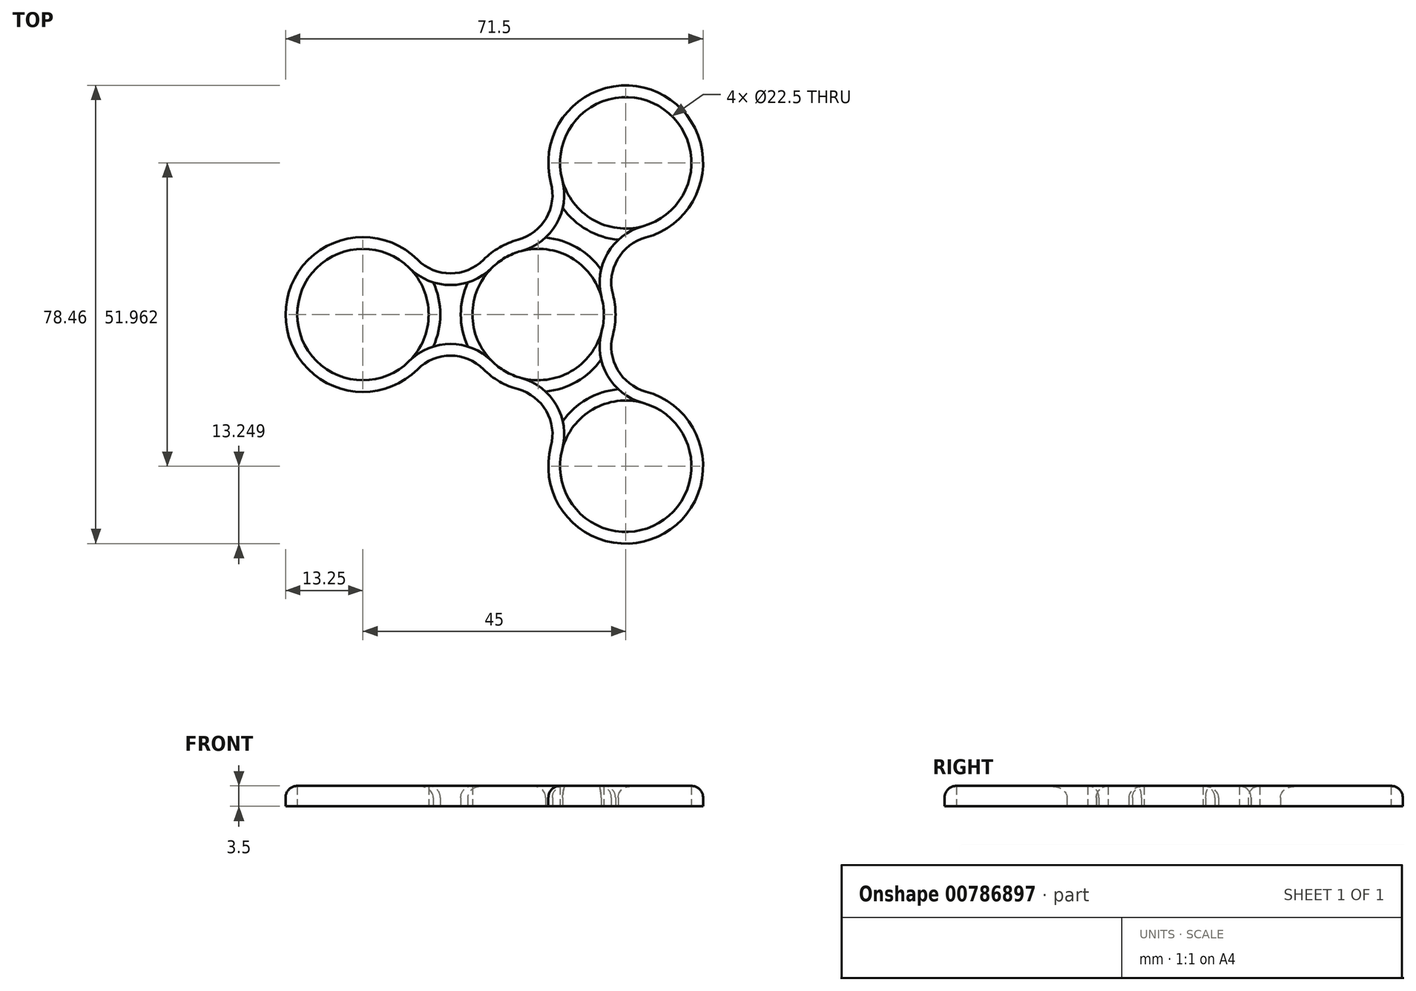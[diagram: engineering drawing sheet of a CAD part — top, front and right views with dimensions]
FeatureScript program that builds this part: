
annotation { "Feature Type Name" : "Feature", "Feature Type Description" : "" }
export const myFeature = defineFeature(function(context is Context, id is Id, definition is map)
    precondition{}
    {
        {
            assignVariable(context, id + "F0", {"name" : "B608_T", "anyValue" : 7});
        }
        {
            var Q0;
            Q0=qCreatedBy(makeId("Top.planeOp"),FACE);
            var sketch = newSketch(context, id + "F1", { "sketchPlane" : qUnion([Q0])});
            skCircle(sketch, "E0", {"center": v(0, 0) * mm, "radius": 11.25 * mm});
            skCircle(sketch, "E1.cCircle", {"center": v(0, 0) * mm, "radius": 15 * mm, "construction": true});
            skLineSegment(sketch, "E1.0", {"start": v(15, 25.98) * mm, "end": v(15, -25.98) * mm, "construction": true});
            skLineSegment(sketch, "E1.1", {"start": v(15, -25.98) * mm, "end": v(-30, 0) * mm, "construction": true});
            skLineSegment(sketch, "E1.2", {"start": v(-30, 0) * mm, "end": v(15, 25.98) * mm, "construction": true});
            skPoint(sketch, "E1.0.midPoint", {"position": v(15, 0) * mm});
            skCircle(sketch, "E2", {"center": v(-30, 0) * mm, "radius": 11.25 * mm});
            skCircle(sketch, "E3", {"center": v(15, -25.98) * mm, "radius": 11.25 * mm});
            skCircle(sketch, "E4", {"center": v(15, 25.98) * mm, "radius": 11.25 * mm});
            skPoint(sketch, "E5.orphan", {"position": v(0, -11.15) * mm});
            skPoint(sketch, "E6.orphan", {"position": v(0, 11.15) * mm});
            skArc(sketch, "E7.0", {"start": v(-17.94, -5.5) * mm, "mid": v(-16.75, 0) * mm, "end": v(-17.94, 5.5) * mm});
            skArc(sketch, "E8.0", {"start": v(2.2, -22.57) * mm, "mid": v(21.62, -37.46) * mm, "end": v(18.45, -13.19) * mm});
            skArc(sketch, "E9.0", {"start": v(18.45, 13.19) * mm, "mid": v(13.9, 39.18) * mm, "end": v(13.73, 12.8) * mm});
            skArc(sketch, "E10.0", {"start": v(-9.35, -9.39) * mm, "mid": v(-6.62, -11.47) * mm, "end": v(-3.45, -12.8) * mm});
            skLineSegment(sketch, "E11", {"start": v(-7.65, -13.25) * mm, "end": v(-7.03, -13.25) * mm});
            skLineSegment(sketch, "E12", {"start": v(-7.65, 13.25) * mm, "end": v(-7.03, 13.25) * mm});
            skLineSegment(sketch, "E13", {"start": v(-7.65, -13.25) * mm, "end": v(-7.96, -12.71) * mm});
            skLineSegment(sketch, "E14", {"start": v(15.3, 0) * mm, "end": v(15, 0.54) * mm});
            skLineSegment(sketch, "E15", {"start": v(-7.96, 12.71) * mm, "end": v(-7.65, 13.25) * mm});
            skLineSegment(sketch, "E16", {"start": v(15, -0.54) * mm, "end": v(15.3, 0) * mm});
            skPoint(sketch, "E17.orphan", {"position": v(0, -13.25) * mm});
            skPoint(sketch, "E18.orphan", {"position": v(0, 13.25) * mm});
            skCircle(sketch, "E19", {"center": v(0, 0) * mm, "radius": 8.5 * mm});
            skCircle(sketch, "E20", {"center": v(-30, 0) * mm, "radius": 8.5 * mm});
            skCircle(sketch, "E21", {"center": v(15, -25.98) * mm, "radius": 8.5 * mm});
            skCircle(sketch, "E22", {"center": v(15, 25.98) * mm, "radius": 8.5 * mm});
            skArc(sketch, "E23", {"start": v(-20.65, 9.39) * mm, "mid": v(-15, 7.05) * mm, "end": v(-9.35, 9.39) * mm});
            skArc(sketch, "E24", {"start": v(-9.35, -9.39) * mm, "mid": v(-15, -7.05) * mm, "end": v(-20.65, -9.39) * mm});
            skArc(sketch, "E25", {"start": v(-3.45, 12.8) * mm, "mid": v(1.4, 16.52) * mm, "end": v(2.2, 22.57) * mm});
            skArc(sketch, "E26", {"start": v(18.45, 13.19) * mm, "mid": v(13.6, 9.46) * mm, "end": v(12.8, 3.4) * mm});
            skArc(sketch, "E27", {"start": v(12.8, -3.4) * mm, "mid": v(13.6, -9.46) * mm, "end": v(18.45, -13.19) * mm});
            skArc(sketch, "E28", {"start": v(2.2, -22.57) * mm, "mid": v(1.4, -16.52) * mm, "end": v(-3.45, -12.8) * mm});
            skPoint(sketch, "E29.orphan", {"position": v(-30, 13.25) * mm});
            skPoint(sketch, "E30.orphan", {"position": v(-30, -13.25) * mm});
            skArc(sketch, "E31.0", {"start": v(-12.06, -5.5) * mm, "mid": v(-15, -5.05) * mm, "end": v(-17.94, -5.5) * mm});
            skArc(sketch, "E32.0", {"start": v(-17.94, 5.5) * mm, "mid": v(-15, 5.05) * mm, "end": v(-12.06, 5.5) * mm});
            skArc(sketch, "E33.trimOffspring", {"start": v(-12.06, 5.5) * mm, "mid": v(-13.25, 0) * mm, "end": v(-12.06, -5.5) * mm});
            skArc(sketch, "E34.trimOffspring", {"start": v(-20.65, 9.39) * mm, "mid": v(-43.25, 0) * mm, "end": v(-20.65, -9.39) * mm});
            skArc(sketch, "E35.trimOffspring", {"start": v(4.21, -18.29) * mm, "mid": v(3.12, -15.52) * mm, "end": v(1.27, -13.19) * mm});
            skArc(sketch, "E36.0", {"start": v(10.79, -7.7) * mm, "mid": v(11.88, -10.46) * mm, "end": v(13.73, -12.8) * mm});
            skArc(sketch, "E37.trimOffspring", {"start": v(1.27, -13.19) * mm, "mid": v(6.63, -11.47) * mm, "end": v(10.79, -7.7) * mm});
            skArc(sketch, "E38.trimOffspring", {"start": v(13.73, -12.8) * mm, "mid": v(8.38, -14.5) * mm, "end": v(4.21, -18.29) * mm});
            skArc(sketch, "E39.trimOffspring", {"start": v(12.8, -3.4) * mm, "mid": v(13.25, 0) * mm, "end": v(12.8, 3.4) * mm});
            skArc(sketch, "E40.0", {"start": v(1.27, 13.19) * mm, "mid": v(3.12, 15.52) * mm, "end": v(4.21, 18.29) * mm});
            skArc(sketch, "E41.trimOffspring", {"start": v(10.79, 7.7) * mm, "mid": v(6.62, 11.47) * mm, "end": v(1.27, 13.19) * mm});
            skArc(sketch, "E42.trimOffspring", {"start": v(13.73, 12.8) * mm, "mid": v(11.88, 10.46) * mm, "end": v(10.79, 7.7) * mm});
            skArc(sketch, "E43.trimOffspring", {"start": v(-3.45, 12.8) * mm, "mid": v(-6.63, 11.47) * mm, "end": v(-9.35, 9.39) * mm});
            skSolve(sketch);
        }
        {
            var Q0;
            Q0=makeQuery(id+"F1.imprint","IMPRINT",FACE,{"disambiguationData":[TD([[makeQuery(id+"F1.imprint","IMPRINT",EDGE,{"derivedFrom":sQuery(id+"F1.wireOp",EDGE,"E10.0")}),-1.0]])]});
            var Q1;
            Q1=makeQuery(id+"F1.imprint","IMPRINT",FACE,{"disambiguationData":[TD([[makeQuery(id+"F1.imprint","IMPRINT",EDGE,{"derivedFrom":sQuery(id+"F1.wireOp",EDGE,"E2")}),-1.0]])]});
            var Q2;
            Q2=makeQuery(id+"F1.imprint","IMPRINT",FACE,{"disambiguationData":[TD([[makeQuery(id+"F1.imprint","IMPRINT",EDGE,{"derivedFrom":sQuery(id+"F1.wireOp",EDGE,"E0")}),-1.0]])]});
            var Q3;
            Q3=makeQuery(id+"F1.imprint","IMPRINT",FACE,{"disambiguationData":[TD([[makeQuery(id+"F1.imprint","IMPRINT",EDGE,{"derivedFrom":sQuery(id+"F1.wireOp",EDGE,"E4")}),-1.0]])]});
            var Q4;
            Q4=makeQuery(id+"F1.imprint","IMPRINT",FACE,{"disambiguationData":[TD([[makeQuery(id+"F1.imprint","IMPRINT",EDGE,{"derivedFrom":sQuery(id+"F1.wireOp",EDGE,"E3")}),-1.0]])]});
            extrude(context, id + "F2", {"entities" : qUnion([Q0, Q1, Q2, Q3, Q4]), "depth" : (getVariable(context, 'B608_T') / 2) * mm, "offsetDistance" : 25 * mm});
        }
        {
            var Q0;
            Q0=makeQuery(id+"F2.opExtrude","CAP_EDGE",EDGE,{"disambiguationData":[OSD([sQuery(id+"F1.wireOp",EDGE,"E8.0")])],"isStart":false});
            var Q1;
            Q1=makeQuery(id+"F2.opExtrude","CAP_EDGE",EDGE,{"disambiguationData":[OSD([sQuery(id+"F1.wireOp",EDGE,"E25")])],"isStart":false});
            var Q2;
            Q2=makeQuery(id+"F2.opExtrude","CAP_EDGE",EDGE,{"disambiguationData":[OSD([sQuery(id+"F1.wireOp",EDGE,"E23")])],"isStart":false});
            var Q3;
            Q3=makeQuery(id+"F2.opExtrude","CAP_EDGE",EDGE,{"disambiguationData":[OSD([sQuery(id+"F1.wireOp",EDGE,"E24")])],"isStart":false});
            var Q4;
            Q4=makeQuery(id+"F2.opExtrude","CAP_EDGE",EDGE,{"disambiguationData":[OSD([sQuery(id+"F1.wireOp",EDGE,"E43.trimOffspring")])],"isStart":false});
            var Q5;
            Q5=makeQuery(id+"F2.opExtrude","CAP_EDGE",EDGE,{"disambiguationData":[OSD([sQuery(id+"F1.wireOp",EDGE,"E26")])],"isStart":false});
            var Q6;
            {var subQ0=sQuery(id+"F1.wireOp",EDGE,"E9.0");Q6=makeQuery(id+"F2.opExtrude","CAP_EDGE",EDGE,{"disambiguationData":[OSD([subQ0]),TDD([makeQuery(id+"F1.imprint","IMPRINT",EDGE,{"disambiguationData":[TD([[makeQuery(id+"F1.imprint","INTERSECT",VERTEX,{"derivedFrom":[subQ0,sQuery(id+"F1.wireOp",EDGE,"E26")]}),-1.0]])],"derivedFrom":subQ0})])],"isStart":false});}
            var Q7;
            Q7=makeQuery(id+"F2.opExtrude","CAP_EDGE",EDGE,{"disambiguationData":[OSD([sQuery(id+"F1.wireOp",EDGE,"E34.trimOffspring")])],"isStart":false});
            var Q8;
            Q8=makeQuery(id+"F2.opExtrude","CAP_EDGE",EDGE,{"disambiguationData":[OSD([sQuery(id+"F1.wireOp",EDGE,"E28")])],"isStart":false});
            var Q9;
            Q9=makeQuery(id+"F2.opExtrude","CAP_EDGE",EDGE,{"disambiguationData":[OSD([sQuery(id+"F1.wireOp",EDGE,"E10.0")])],"isStart":false});
            var Q10;
            Q10=makeQuery(id+"F2.opExtrude","CAP_EDGE",EDGE,{"disambiguationData":[OSD([sQuery(id+"F1.wireOp",EDGE,"E27")])],"isStart":false});
            var Q11;
            Q11=makeQuery(id+"F2.opExtrude","CAP_EDGE",EDGE,{"disambiguationData":[OSD([sQuery(id+"F1.wireOp",EDGE,"E39.trimOffspring")])],"isStart":false});
            fillet(context, id + "F3", {"entities" : qUnion([Q0, Q1, Q2, Q3, Q4, Q5, Q6, Q7, Q8, Q9, Q10, Q11]), "radius" : 2 * mm, "tangentPropagation" : true, "allowEdgeOverflow" : false});
        }
        {
            var Q0;
            Q0=makeQuery(id+"F2.opExtrude","CAP_EDGE",EDGE,{"disambiguationData":[OSD([sQuery(id+"F1.wireOp",EDGE,"E41.trimOffspring")])],"isStart":false});
            var Q1;
            Q1=makeQuery(id+"F2.opExtrude","CAP_EDGE",EDGE,{"disambiguationData":[OSD([sQuery(id+"F1.wireOp",EDGE,"E37.trimOffspring")])],"isStart":false});
            var Q2;
            Q2=makeQuery(id+"F2.opExtrude","CAP_EDGE",EDGE,{"disambiguationData":[OSD([sQuery(id+"F1.wireOp",EDGE,"E33.trimOffspring")])],"isStart":false});
            var Q3;
            {var subQ0=sQuery(id+"F1.wireOp",EDGE,"E9.0");Q3=makeQuery(id+"F2.opExtrude","CAP_EDGE",EDGE,{"disambiguationData":[OSD([subQ0]),TDD([makeQuery(id+"F1.imprint","IMPRINT",EDGE,{"disambiguationData":[TD([[makeQuery(id+"F1.imprint","INTERSECT",VERTEX,{"derivedFrom":[subQ0,sQuery(id+"F1.wireOp",EDGE,"E42.trimOffspring")]}),1.0]])],"derivedFrom":subQ0})])],"isStart":false});}
            var Q4;
            Q4=makeQuery(id+"F2.opExtrude","CAP_EDGE",EDGE,{"disambiguationData":[OSD([sQuery(id+"F1.wireOp",EDGE,"E7.0")])],"isStart":false});
            var Q5;
            Q5=makeQuery(id+"F2.opExtrude","CAP_EDGE",EDGE,{"disambiguationData":[OSD([sQuery(id+"F1.wireOp",EDGE,"E38.trimOffspring")])],"isStart":false});
            fillet(context, id + "F4", {"entities" : qUnion([Q0, Q1, Q2, Q3, Q4, Q5]), "radius" : 2 * mm, "tangentPropagation" : true, "allowEdgeOverflow" : false});
        }
    });
